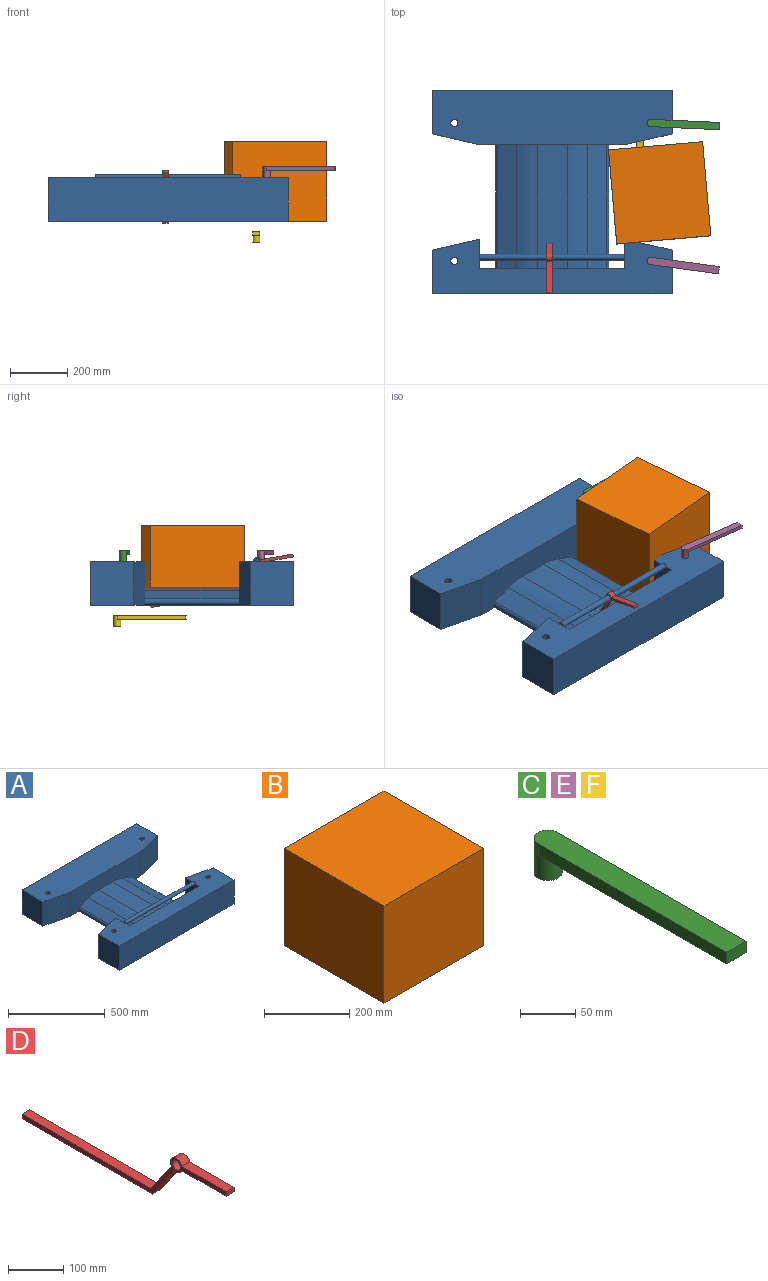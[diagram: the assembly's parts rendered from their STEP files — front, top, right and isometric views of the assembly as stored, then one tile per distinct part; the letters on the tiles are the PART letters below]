
ASSEMBLY  parts=6 mates=4
PART A: 229 faces, bbox 838.2x711.2x162.4 mm
  f0: plane 152.4x101.6mm, normal (1,0,0), area 15326.8mm2, adj f2,f4,f201,f223,f225
  f1: plane 152.4x101.6mm, normal (-1,0,0), area 15326.8mm2, adj f2,f4,f181,f223,f225
  f2: plane 838.2x190.5mm, normal (0,0,1), area 100760.6mm2, adj f0,f1,f179,f180,f181,f201,f212,f220
  f3: plane 838.2x190.5mm, normal (0,0,1), area 152373.2mm2, adj f5,f6,f7,f8,f9,f10,f11,f12
  f4: plane 838.2x711.2mm, normal (0,0,-1), area 413419.6mm2, adj f0,f1,f5,f6,f7,f8,f9,f10
  f5: plane 508x152.4mm, normal (0,-1,0), area 57102.1mm2, adj f3,f4,f182,f200,f214,f215,f216,f217
  f6: plane 152.4x0.09mm, normal (-1,0,0), area 14mm2, adj f3,f4,f7,f213
  f7: plane 152.4x0.03mm, normal (0,1,0), area 3.8mm2, adj f3,f4,f6,f8
  f8: plane 152.4x0.21mm, normal (1,0,0), area 32.6mm2, adj f3,f4,f7,f9
  f9: plane 152.4x0.12mm, normal (0,-1,0), area 18.2mm2, adj f3,f4,f8,f10
  f10: plane 152.4x0.02mm, normal (-1,0,0), area 3.4mm2, adj f3,f4,f9,f11
  f11: plane 152.4x0.09mm, normal (0,1,0), area 14.4mm2, adj f3,f4,f10,f12
  f12: plane 152.4x0.08mm, normal (-1,0,0), area 11.9mm2, adj f3,f4,f11,f13
  f13: plane 152.4x0.09mm, normal (0,-1,0), area 13.5mm2, adj f3,f4,f12,f14
  f14: plane 152.4x0.02mm, normal (-1,0,0), area 3.4mm2, adj f3,f4,f13,f213
  f15: extruded ~152.4x0.03mm, area 4.6mm2, adj f3,f4,f16,f202
  f16: extruded ~152.4x0.02mm, area 3mm2, adj f3,f4,f15,f17
  f17: plane 152.4x0.02mm, normal (-0.99,0.15,0), area 3.5mm2, adj f3,f4,f16,f18
  f18: extruded ~152.4x0.02mm, area 2.7mm2, adj f3,f4,f17,f19
  f19: extruded ~152.4x0.03mm, area 5.8mm2, adj f3,f4,f18,f20
  f20: extruded ~152.4x0.04mm, area 6.5mm2, adj f3,f4,f19,f21
  f21: plane 152.4x0.09mm, normal (-1,0,0), area 13.1mm2, adj f3,f4,f20,f22
  f22: plane 152.4x0.02mm, normal (0,1,0), area 3.7mm2, adj f3,f4,f21,f23
  f23: plane 152.4x0.16mm, normal (1,0,0), area 24.5mm2, adj f3,f4,f22,f24
  f24: plane 152.4x0.02mm, normal (0,-1,0), area 3.1mm2, adj f3,f4,f23,f25
  f25: plane 152.4x0.03mm, normal (-1,-0.09,0), area 4.5mm2, adj f3,f4,f24,f26
  f26: plane 152.4x0mm, normal (0,-1,0), area 0.2mm2, adj f3,f4,f25,f202
  f27: plane 152.4x0.02mm, normal (0,1,0), area 2.8mm2, adj f3,f4,f28,f203
  f28: plane 152.4x0.02mm, normal (0.98,0.21,0), area 3.6mm2, adj f3,f4,f27,f29
  f29: plane 152.4x0mm, normal (0,1,0), area 0.2mm2, adj f3,f4,f28,f30
  f30: extruded ~152.4x0.02mm, area 4.9mm2, adj f3,f4,f29,f31
  f31: extruded ~152.4x0.03mm, area 4.7mm2, adj f3,f4,f30,f32
  f32: extruded ~152.4x0.04mm, area 6.1mm2, adj f3,f4,f31,f33
  f33: extruded ~152.4x0.04mm, area 5.9mm2, adj f3,f4,f32,f34
  f34: extruded ~152.4x0.08mm, area 15.9mm2, adj f3,f4,f33,f35
  f35: plane 152.4x0.03mm, normal (0.03,-1,0), area 4.2mm2, adj f3,f4,f34,f36
  f36: plane 152.4x0.01mm, normal (1,0,0), area 1.5mm2, adj f3,f4,f35,f37
  f37: extruded ~152.4x0.03mm, area 4.6mm2, adj f3,f4,f36,f38
  f38: extruded ~152.4x0.03mm, area 4.3mm2, adj f3,f4,f37,f39
  f39: extruded ~152.4x0.05mm, area 7.2mm2, adj f3,f4,f38,f40
  f40: plane 152.4x0.02mm, normal (0.93,0.37,0), area 3.1mm2, adj f3,f4,f39,f41
  f41: extruded ~152.4x0.03mm, area 4.3mm2, adj f3,f4,f40,f42
  f42: extruded ~152.4x0.03mm, area 4.4mm2, adj f3,f4,f41,f43
  f43: extruded ~152.4x0.04mm, area 6.9mm2, adj f3,f4,f42,f44
  f44: extruded ~152.4x0.04mm, area 6.8mm2, adj f3,f4,f43,f203
  f45: plane 152.4x0.02mm, normal (0,1,0), area 3.7mm2, adj f3,f4,f46,f204
  f46: plane 152.4x0.1mm, normal (1,0,0), area 15.9mm2, adj f3,f4,f45,f47
  f47: extruded ~152.4x0.03mm, area 4.7mm2, adj f3,f4,f46,f48
  f48: extruded ~152.4x0.03mm, area 4.3mm2, adj f3,f4,f47,f49
  f49: extruded ~152.4x0.03mm, area 5.7mm2, adj f3,f4,f48,f50
  f50: extruded ~152.4x0.04mm, area 6.5mm2, adj f3,f4,f49,f51
  f51: plane 152.4x0.09mm, normal (-1,0,0), area 13.7mm2, adj f3,f4,f50,f52
  f52: plane 152.4x0.02mm, normal (0,1,0), area 3.7mm2, adj f3,f4,f51,f53
  f53: plane 152.4x0.1mm, normal (1,0,0), area 15.9mm2, adj f3,f4,f52,f54
  f54: extruded ~152.4x0.03mm, area 4.7mm2, adj f3,f4,f53,f55
  f55: extruded ~152.4x0.03mm, area 4.3mm2, adj f3,f4,f54,f56
  f56: extruded ~152.4x0.03mm, area 5.7mm2, adj f3,f4,f55,f57
  f57: extruded ~152.4x0.05mm, area 7.2mm2, adj f3,f4,f56,f58
  f58: plane 152.4x0.08mm, normal (-1,0,0), area 12.8mm2, adj f3,f4,f57,f59
  f59: plane 152.4x0.02mm, normal (0,1,0), area 3.7mm2, adj f3,f4,f58,f60
  f60: plane 152.4x0.16mm, normal (1,0,0), area 24.5mm2, adj f3,f4,f59,f61
  f61: plane 152.4x0.02mm, normal (0,-1,0), area 3mm2, adj f3,f4,f60,f62
  f62: plane 152.4x0.02mm, normal (-0.98,-0.18,0), area 3.4mm2, adj f3,f4,f61,f63
  f63: plane 152.4x0mm, normal (0,-1,0), area 0.2mm2, adj f3,f4,f62,f64
  f64: extruded ~152.4x0.02mm, area 4.2mm2, adj f3,f4,f63,f65
  f65: extruded ~152.4x0.03mm, area 4.5mm2, adj f3,f4,f64,f66
  f66: extruded ~152.4x0.05mm, area 9.2mm2, adj f3,f4,f65,f67
  f67: plane 152.4x0mm, normal (0,-1,0), area 0.2mm2, adj f3,f4,f66,f68
  f68: extruded ~152.4x0.02mm, area 4.5mm2, adj f3,f4,f67,f69
  f69: extruded ~152.4x0.03mm, area 4.9mm2, adj f3,f4,f68,f70
  f70: extruded ~152.4x0.04mm, area 6.8mm2, adj f3,f4,f69,f71
  f71: extruded ~152.4x0.04mm, area 7.3mm2, adj f3,f4,f70,f204
  f72: plane 152.4x0.02mm, normal (0,1,0), area 2.8mm2, adj f3,f4,f73,f205
  f73: plane 152.4x0.02mm, normal (0.98,0.21,0), area 3.6mm2, adj f3,f4,f72,f74
  f74: plane 152.4x0mm, normal (0,1,0), area 0.2mm2, adj f3,f4,f73,f75
  f75: extruded ~152.4x0.02mm, area 4.9mm2, adj f3,f4,f74,f76
  f76: extruded ~152.4x0.03mm, area 4.7mm2, adj f3,f4,f75,f77
  f77: extruded ~152.4x0.04mm, area 6.1mm2, adj f3,f4,f76,f78
  f78: extruded ~152.4x0.04mm, area 5.9mm2, adj f3,f4,f77,f79
  f79: extruded ~152.4x0.08mm, area 15.9mm2, adj f3,f4,f78,f80
  f80: plane 152.4x0.03mm, normal (0.03,-1,0), area 4.2mm2, adj f3,f4,f79,f81
  f81: plane 152.4x0.01mm, normal (1,0,0), area 1.5mm2, adj f3,f4,f80,f82
  f82: extruded ~152.4x0.03mm, area 4.6mm2, adj f3,f4,f81,f83
  f83: extruded ~152.4x0.03mm, area 4.3mm2, adj f3,f4,f82,f84
  f84: extruded ~152.4x0.05mm, area 7.2mm2, adj f3,f4,f83,f85
  f85: plane 152.4x0.02mm, normal (0.93,0.37,0), area 3.1mm2, adj f3,f4,f84,f86
  f86: extruded ~152.4x0.03mm, area 4.3mm2, adj f3,f4,f85,f87
  f87: extruded ~152.4x0.03mm, area 4.4mm2, adj f3,f4,f86,f88
  f88: extruded ~152.4x0.04mm, area 6.9mm2, adj f3,f4,f87,f89
  f89: extruded ~152.4x0.04mm, area 6.8mm2, adj f3,f4,f88,f205
  f90: extruded ~152.4x0.06mm, area 9.9mm2, adj f3,f4,f91,f206
  f91: extruded ~152.4x0.06mm, area 10mm2, adj f3,f4,f90,f92
  f92: extruded ~152.4x0.05mm, area 9.3mm2, adj f3,f4,f91,f93
  f93: extruded ~152.4x0.04mm, area 6.1mm2, adj f3,f4,f92,f94
  f94: extruded ~152.4x0.03mm, area 6mm2, adj f3,f4,f93,f95
  f95: extruded ~152.4x0.04mm, area 6.9mm2, adj f3,f4,f94,f96
  f96: extruded ~152.4x0.06mm, area 10mm2, adj f3,f4,f95,f97
  f97: extruded ~152.4x0.05mm, area 9.2mm2, adj f3,f4,f96,f206
  f98: plane 152.4x0.02mm, normal (0,1,0), area 3.7mm2, adj f3,f4,f99,f207
  f99: plane 152.4x0.1mm, normal (1,0,0), area 15.9mm2, adj f3,f4,f98,f100
  f100: extruded ~152.4x0.03mm, area 4.7mm2, adj f3,f4,f99,f101
  f101: extruded ~152.4x0.03mm, area 4.3mm2, adj f3,f4,f100,f102
  f102: extruded ~152.4x0.03mm, area 5.7mm2, adj f3,f4,f101,f103
  f103: extruded ~152.4x0.04mm, area 6.5mm2, adj f3,f4,f102,f104
  f104: plane 152.4x0.09mm, normal (-1,0,0), area 13.7mm2, adj f3,f4,f103,f105
  f105: plane 152.4x0.02mm, normal (0,1,0), area 3.7mm2, adj f3,f4,f104,f106
  f106: plane 152.4x0.1mm, normal (1,0,0), area 15.9mm2, adj f3,f4,f105,f107
  f107: extruded ~152.4x0.03mm, area 4.7mm2, adj f3,f4,f106,f108
  f108: extruded ~152.4x0.03mm, area 4.3mm2, adj f3,f4,f107,f109
  f109: extruded ~152.4x0.03mm, area 5.7mm2, adj f3,f4,f108,f110
  f110: extruded ~152.4x0.05mm, area 7.2mm2, adj f3,f4,f109,f111
  f111: plane 152.4x0.08mm, normal (-1,0,0), area 12.8mm2, adj f3,f4,f110,f112
  f112: plane 152.4x0.02mm, normal (0,1,0), area 3.7mm2, adj f3,f4,f111,f113
  f113: plane 152.4x0.16mm, normal (1,0,0), area 24.5mm2, adj f3,f4,f112,f114
  f114: plane 152.4x0.02mm, normal (0,-1,0), area 3mm2, adj f3,f4,f113,f115
  f115: plane 152.4x0.02mm, normal (-0.98,-0.18,0), area 3.4mm2, adj f3,f4,f114,f116
  f116: plane 152.4x0mm, normal (0,-1,0), area 0.2mm2, adj f3,f4,f115,f117
  f117: extruded ~152.4x0.02mm, area 4.2mm2, adj f3,f4,f116,f118
  f118: extruded ~152.4x0.03mm, area 4.5mm2, adj f3,f4,f117,f119
  f119: extruded ~152.4x0.05mm, area 9.2mm2, adj f3,f4,f118,f120
  f120: plane 152.4x0mm, normal (0,-1,0), area 0.2mm2, adj f3,f4,f119,f121
  f121: extruded ~152.4x0.02mm, area 4.5mm2, adj f3,f4,f120,f122
  f122: extruded ~152.4x0.03mm, area 4.9mm2, adj f3,f4,f121,f123
  f123: extruded ~152.4x0.04mm, area 6.8mm2, adj f3,f4,f122,f124
  f124: extruded ~152.4x0.04mm, area 7.3mm2, adj f3,f4,f123,f207
  f125: plane 152.4x0.16mm, normal (-1,0,0), area 24.5mm2, adj f3,f4,f126,f208
  f126: plane 152.4x0.02mm, normal (0,1,0), area 3.7mm2, adj f3,f4,f125,f127
  f127: plane 152.4x0.16mm, normal (1,0,0), area 24.5mm2, adj f3,f4,f126,f208
  f128: plane 152.4x0.08mm, normal (0.81,-0.58,0), area 15.4mm2, adj f3,f4,f129,f209
  f129: plane 152.4x0.08mm, normal (0.81,0.58,0), area 14.7mm2, adj f3,f4,f128,f130
  f130: plane 152.4x0.03mm, normal (0,-1,0), area 4.2mm2, adj f3,f4,f129,f131
  f131: plane 152.4x0.06mm, normal (-0.82,-0.57,0), area 11.4mm2, adj f3,f4,f130,f132
  f132: plane 152.4x0.06mm, normal (0.82,-0.57,0), area 11.4mm2, adj f3,f4,f131,f133
  f133: plane 152.4x0.03mm, normal (0,-1,0), area 4.2mm2, adj f3,f4,f132,f134
  f134: plane 152.4x0.08mm, normal (-0.81,0.58,0), area 14.7mm2, adj f3,f4,f133,f135
  f135: plane 152.4x0.08mm, normal (-0.81,-0.58,0), area 15.4mm2, adj f3,f4,f134,f136
  f136: plane 152.4x0.03mm, normal (0,1,0), area 4.2mm2, adj f3,f4,f135,f137
  f137: plane 152.4x0.07mm, normal (0.82,0.57,0), area 12.1mm2, adj f3,f4,f136,f138
  f138: plane 152.4x0.07mm, normal (-0.82,0.57,0), area 12.1mm2, adj f3,f4,f137,f209
  f139: extruded ~152.4x0.03mm, area 4.3mm2, adj f3,f4,f140,f210
  f140: extruded ~152.4x0.06mm, area 9.4mm2, adj f3,f4,f139,f141
  f141: extruded ~152.4x0.06mm, area 9.9mm2, adj f3,f4,f140,f142
  f142: extruded ~152.4x0.06mm, area 10.1mm2, adj f3,f4,f141,f143
  f143: extruded ~152.4x0.05mm, area 8.9mm2, adj f3,f4,f142,f144
  f144: extruded ~152.4x0.05mm, area 8.1mm2, adj f3,f4,f143,f145
  f145: extruded ~152.4x0.05mm, area 8.6mm2, adj f3,f4,f144,f146
  f146: plane 152.4x0.02mm, normal (-1,0,0), area 2.3mm2, adj f3,f4,f145,f147
  f147: plane 152.4x0.11mm, normal (0,1,0), area 16.9mm2, adj f3,f4,f146,f148
  f148: extruded ~152.4x0.04mm, area 7mm2, adj f3,f4,f147,f149
  f149: extruded ~152.4x0.04mm, area 6.4mm2, adj f3,f4,f148,f150
  f150: extruded ~152.4x0.05mm, area 8mm2, adj f3,f4,f149,f151
  f151: plane 152.4x0.02mm, normal (-1,0,0), area 3.3mm2, adj f3,f4,f150,f210
  f152: plane 152.4x0.02mm, normal (0,1,0), area 3.7mm2, adj f3,f4,f153,f211
  f153: plane 152.4x0.1mm, normal (1,0,0), area 15.9mm2, adj f3,f4,f152,f154
  f154: extruded ~152.4x0.03mm, area 4.7mm2, adj f3,f4,f153,f155
  f155: extruded ~152.4x0.03mm, area 4.3mm2, adj f3,f4,f154,f156
  f156: extruded ~152.4x0.03mm, area 5.7mm2, adj f3,f4,f155,f157
  f157: extruded ~152.4x0.04mm, area 6.5mm2, adj f3,f4,f156,f158
  f158: plane 152.4x0.09mm, normal (-1,0,0), area 13.7mm2, adj f3,f4,f157,f159
  f159: plane 152.4x0.02mm, normal (0,1,0), area 3.7mm2, adj f3,f4,f158,f160
  f160: plane 152.4x0.1mm, normal (1,0,0), area 15.9mm2, adj f3,f4,f159,f161
  f161: extruded ~152.4x0.03mm, area 4.7mm2, adj f3,f4,f160,f162
  f162: extruded ~152.4x0.03mm, area 4.3mm2, adj f3,f4,f161,f163
  f163: extruded ~152.4x0.03mm, area 5.7mm2, adj f3,f4,f162,f164
  f164: extruded ~152.4x0.05mm, area 7.2mm2, adj f3,f4,f163,f165
  f165: plane 152.4x0.08mm, normal (-1,0,0), area 12.8mm2, adj f3,f4,f164,f166
  f166: plane 152.4x0.02mm, normal (0,1,0), area 3.7mm2, adj f3,f4,f165,f167
  f167: plane 152.4x0.16mm, normal (1,0,0), area 24.5mm2, adj f3,f4,f166,f168
  f168: plane 152.4x0.02mm, normal (0,-1,0), area 3mm2, adj f3,f4,f167,f169
  f169: plane 152.4x0.02mm, normal (-0.98,-0.18,0), area 3.4mm2, adj f3,f4,f168,f170
  f170: plane 152.4x0mm, normal (0,-1,0), area 0.2mm2, adj f3,f4,f169,f171
  f171: extruded ~152.4x0.02mm, area 4.2mm2, adj f3,f4,f170,f172
  f172: extruded ~152.4x0.03mm, area 4.5mm2, adj f3,f4,f171,f173
  f173: extruded ~152.4x0.05mm, area 9.2mm2, adj f3,f4,f172,f174
  f174: plane 152.4x0mm, normal (0,-1,0), area 0.2mm2, adj f3,f4,f173,f175
  f175: extruded ~152.4x0.02mm, area 4.5mm2, adj f3,f4,f174,f176
  f176: extruded ~152.4x0.03mm, area 4.9mm2, adj f3,f4,f175,f177
  f177: extruded ~152.4x0.04mm, area 6.8mm2, adj f3,f4,f176,f178
  f178: extruded ~152.4x0.04mm, area 7.3mm2, adj f3,f4,f177,f211
  f179: plane 838.2x152.4mm, normal (0,-1,0), area 127741.7mm2, adj f2,f4,f180,f212
  f180: plane 152.4x152.4mm, normal (1,0,0), area 23225.8mm2, adj f2,f4,f179,f181
  f181: plane 165.1x152.4mm, normal (0.22,0.97,0), area 25822.5mm2, adj f1,f2,f4,f180
  f182: plane 165.1x152.4mm, normal (0.22,-0.97,0), area 25822.5mm2, adj f3,f4,f5,f183
  f183: plane 152.4x152.4mm, normal (1,0,0), area 23225.8mm2, adj f3,f4,f182,f184
  f184: plane 418.54x152.4mm, normal (0,1,0), area 63784.7mm2, adj f3,f4,f183,f185
  f185: extruded ~152.4x0.01mm, area 2mm2, adj f3,f4,f184,f186
  f186: extruded ~152.4x0.01mm, area 2.1mm2, adj f3,f4,f185,f187
  f187: extruded ~152.4x0.01mm, area 1.7mm2, adj f3,f4,f186,f188
  f188: extruded ~152.4x0.01mm, area 1.8mm2, adj f3,f4,f187,f189
  f189: extruded ~152.4x0.01mm, area 2.1mm2, adj f3,f4,f188,f190
  f190: extruded ~152.4x0.01mm, area 2mm2, adj f3,f4,f189,f191
  f191: plane 152.4x0.24mm, normal (0,1,0), area 36.3mm2, adj f3,f4,f190,f192
  f192: extruded ~152.4x0.01mm, area 2.6mm2, adj f3,f4,f191,f193
  f193: extruded ~152.4x0.02mm, area 4.7mm2, adj f3,f4,f192,f194
  f194: plane 152.4x0.02mm, normal (0,1,0), area 2.5mm2, adj f3,f4,f193,f195
  f195: plane 152.4x0mm, normal (1,0,0), area 0.6mm2, adj f3,f4,f194,f196
  f196: extruded ~152.4x0.02mm, area 4.1mm2, adj f3,f4,f195,f197
  f197: extruded ~152.4x0.01mm, area 1.5mm2, adj f3,f4,f196,f198
  f198: plane 419.38x152.4mm, normal (0,1,0), area 63913mm2, adj f3,f4,f197,f199
  f199: plane 152.4x152.4mm, normal (-1,0,0), area 23225.8mm2, adj f3,f4,f198,f200
  f200: plane 165.1x152.4mm, normal (-0.22,-0.97,0), area 25822.5mm2, adj f3,f4,f5,f199
  f201: plane 165.1x152.4mm, normal (-0.22,0.97,0), area 25822.5mm2, adj f0,f2,f4,f212
  f202: extruded ~152.4x0.02mm, area 5mm2, adj f3,f4,f15,f26
  f203: plane 152.4x0.11mm, normal (-1,0,0), area 16.7mm2, adj f3,f4,f27,f44
  f204: plane 152.4x0.1mm, normal (-1,0,0), area 16mm2, adj f3,f4,f45,f71
  f205: plane 152.4x0.11mm, normal (-1,0,0), area 16.7mm2, adj f3,f4,f72,f89
  f206: extruded ~152.4x0.05mm, area 9.1mm2, adj f3,f4,f90,f97
  f207: plane 152.4x0.1mm, normal (-1,0,0), area 16mm2, adj f3,f4,f98,f124
  f208: plane 152.4x0.02mm, normal (0,-1,0), area 3.7mm2, adj f3,f4,f125,f127
  f209: plane 152.4x0.03mm, normal (0,1,0), area 4.2mm2, adj f3,f4,f128,f138
  f210: extruded ~152.4x0.02mm, area 4mm2, adj f3,f4,f139,f151
  f211: plane 152.4x0.1mm, normal (-1,0,0), area 16mm2, adj f3,f4,f152,f178
  f212: plane 152.4x152.4mm, normal (-1,0,0), area 23225.8mm2, adj f2,f4,f179,f201
  f213: plane 152.4x0.09mm, normal (0,1,0), area 13.5mm2, adj f3,f4,f6,f14
  f214: plane 431.8x103.53mm, normal (0,0,1), area 44703.8mm2, adj f5,f223,f227,f228
  f215: plane 431.8x66.6mm, normal (0.36,0,0.93), area 30811.9mm2, adj f5,f217,f223,f227
  f216: plane 431.8x66.6mm, normal (-0.36,0,0.93), area 30811.9mm2, adj f5,f218,f223,f228
  f217: cylinder r=12.7mm len=431.8mm, axis (0,-1,0), area 15214.5mm2, adj f4,f5,f215,f223
  f218: cylinder r=12.7mm len=431.8mm, axis (0,1,0), area 15214.5mm2, adj f4,f5,f216,f223
  f219: cylinder r=12.7mm len=152.4mm, axis (0,0,1), area 12161mm2, adj f3,f4
  f220: cylinder r=12.7mm len=152.4mm, axis (0,0,1), area 12161mm2, adj f2,f4
  f221: cylinder r=12.7mm len=152.4mm, axis (0,0,1), area 12161mm2, adj f2,f4
  f222: cylinder r=12.7mm len=152.4mm, axis (0,0,1), area 12161mm2, adj f3,f4
  f223: plane 508x152.4mm, normal (0,1,0), area 57102.1mm2, adj f0,f1,f2,f4,f214,f215,f216,f217
  f224: plane 20x10mm, normal (1,0,0), area 157.1mm2, adj f2,f225
  f225: cylinder r=10mm len=508mm, axis (-1,0,0), area 31918.6mm2, adj f0,f1,f224,f226
  f226: plane 20x10mm, normal (-1,0,0), area 157.1mm2, adj f2,f225
  f227: cylinder r=200mm len=431.8mm, axis (0,-1,0), area 31709.1mm2, adj f5,f214,f215,f223
  f228: cylinder r=200mm len=431.8mm, axis (0,1,0), area 31709.1mm2, adj f5,f214,f216,f223
PART B: 6 faces, bbox 330.2x330.2x279.4 mm
  f0: plane 330.2x279.4mm, normal (1,0,0), area 92257.9mm2, adj f1,f3,f4,f5
  f1: plane 330.2x279.4mm, normal (0,1,0), area 92257.9mm2, adj f0,f2,f4,f5
  f2: plane 330.2x279.4mm, normal (-1,0,0), area 92257.9mm2, adj f1,f3,f4,f5
  f3: plane 330.2x279.4mm, normal (0,-1,0), area 92257.9mm2, adj f0,f2,f4,f5
  f4: plane 330.2x330.2mm, normal (0,0,1), area 109032mm2, adj f0,f1,f2,f3
  f5: plane 330.2x330.2mm, normal (0,0,-1), area 109032mm2, adj f0,f1,f2,f3
PART C: 7 faces, bbox 25.4x254x38.1 mm
  f0: cylinder r=12.7mm len=38.1mm, axis (0,0,-1), area 2533.5mm2, adj f1,f2,f3,f4,f6
  f1: plane 25.4x25.4mm, normal (0,0,-1), area 506.7mm2, adj f0
  f2: plane 241.3x25.4mm, normal (0,0,-1), area 5872.8mm2, adj f0,f3,f4,f5
  f3: plane 240.97x12.7mm, normal (1,0,0), area 3060.3mm2, adj f0,f2,f5,f6
  f4: plane 240.97x12.7mm, normal (-1,0,0), area 3060.3mm2, adj f0,f2,f5,f6
  f5: cylinder r=241.3mm len=25.4mm, axis (0,0,-1), area 322.7mm2, adj f2,f3,f4,f6
  f6: plane 254x25.4mm, normal (0,0,1), area 6379.5mm2, adj f0,f3,f4,f5
PART D: 13 faces, bbox 20x520.7x108.9 mm
  f0: plane 20x10mm, normal (0,-1,0), area 200mm2, adj f1,f9,f11,f12
  f1: plane 112.86x20mm, normal (0,0,-1), area 2257.2mm2, adj f0,f2,f11,f12
  f2: cylinder r=15mm len=20mm, axis (-1,0,0), area 453.4mm2, adj f1,f3,f11,f12
  f3: plane 79.49x56.78mm, normal (0,-0.81,-0.58), area 1953.6mm2, adj f2,f4,f11,f12
  f4: plane 332.77x20mm, normal (0,0,-1), area 6655.5mm2, adj f3,f5,f11,f12
  f5: plane 20x10mm, normal (0,1,0), area 200mm2, adj f4,f6,f11,f12
  f6: plane 327.63x20mm, normal (0,0,1), area 6552.5mm2, adj f5,f7,f11,f12
  f7: plane 75.3x53.78mm, normal (0,0.81,0.58), area 1850.7mm2, adj f6,f8,f11,f12
  f8: cylinder r=15mm len=29.14mm, axis (-1,0,0), area 1023.7mm2, adj f7,f9,f11,f12
  f9: plane 112.86x20mm, normal (0,0,1), area 2257.2mm2, adj f0,f8,f11,f12
  f10: cylinder r=10mm len=20mm, axis (-1,0,0), area 1256.6mm2, adj f11,f12
  f11: plane 520.7x108.9mm, normal (1,0,0), area 5762.8mm2, adj f0,f1,f2,f3,f4,f5,f6,f7
  f12: plane 520.7x108.9mm, normal (-1,0,0), area 5762.8mm2, adj f0,f1,f2,f3,f4,f5,f6,f7
PART E: same geometry as C
PART F: same geometry as C
PLACE A t=(0,-7.26,-25.4)mm
PLACE B rot(axis=(0,0,1),95deg) t=(397.88,-263.57,0)mm
PLACE C rot(axis=(0,0,1),87.4deg) t=(569.5,-120.58,-25.4)mm
PLACE D rot(axis=(-1,0,0),9.9deg) t=(-464.1,-41.23,-62.06)mm
PLACE E rot(axis=(0,0,1),82.2deg) t=(536.44,-622.15,-25.4)mm
PLACE F t=(-36.54,13.43,-252.51)mm
MATE revolute E.f0 <-> A.f220  axis (0,0,-1) through (344.04,-248.56,152.4)mm
MATE revolute C.f0 <-> A.f219  axis (0,0,-1) through (344.04,234.04,152.4)mm
MATE revolute D.f2 <-> A.f225  axis (1,0,0) through (0,-235.86,152.4)mm
MATE planar A.f4 <-> B.f5  axis (0,0,-1) through (0,0,0)mm
